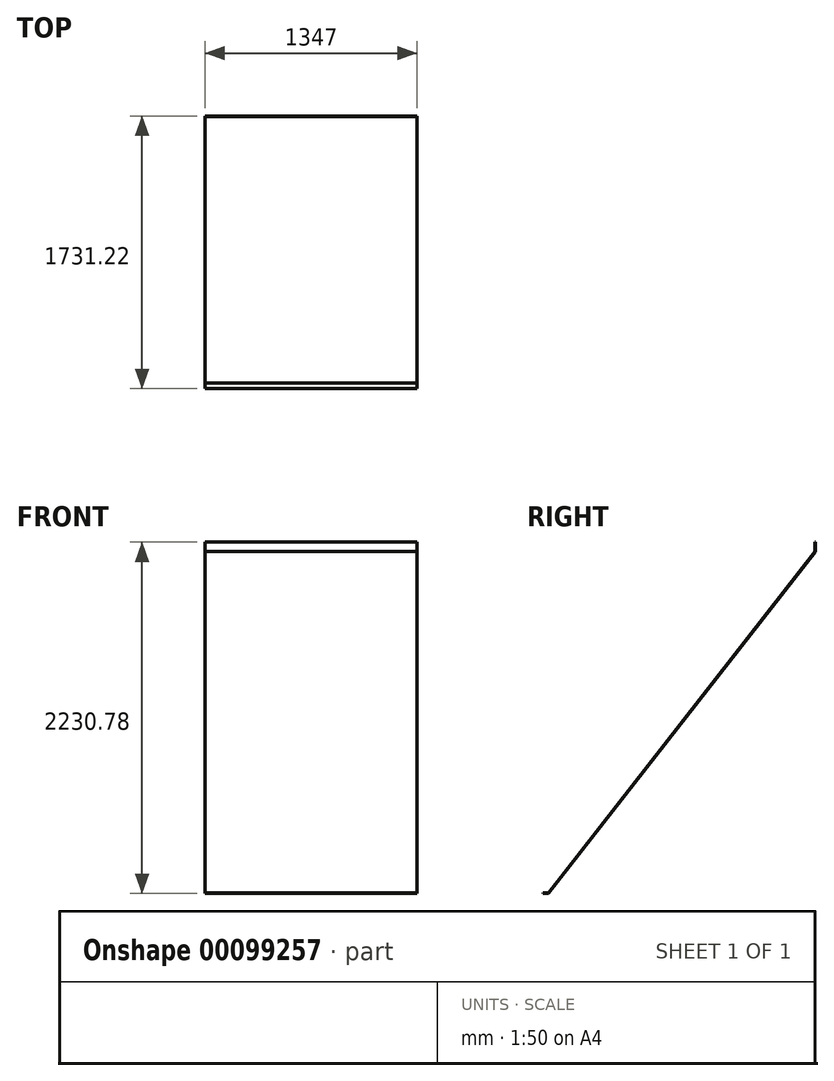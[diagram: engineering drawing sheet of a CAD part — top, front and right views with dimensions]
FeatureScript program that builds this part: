
annotation { "Feature Type Name" : "Feature", "Feature Type Description" : "" }
export const myFeature = defineFeature(function(context is Context, id is Id, definition is map)
    precondition{}
    {
        {
            var Q0;
            Q0=qCreatedBy(makeId("Right.planeOp"),FACE);
            var sketch = newSketch(context, id + "F0", { "sketchPlane" : qUnion([Q0])});
            skLineSegment(sketch, "E0", {"start": v(-36, 0) * mm, "end": v(0, 0) * mm});
            skLineSegment(sketch, "E1", {"start": v(0, 0) * mm, "end": v(1695.22, 2169.78) * mm});
            skLineSegment(sketch, "E2", {"start": v(1695.22, 2169.78) * mm, "end": v(1695.22, 2230.78) * mm});
            skLineSegment(sketch, "E3.0", {"start": v(-1.46, 3) * mm, "end": v(1692.22, 2170.82) * mm});
            skLineSegment(sketch, "E4.0", {"start": v(1692.22, 2170.82) * mm, "end": v(1692.22, 2230.78) * mm});
            skLineSegment(sketch, "E5.0", {"start": v(-36, 3) * mm, "end": v(-1.46, 3) * mm});
            skLineSegment(sketch, "E6", {"start": v(-36, 0) * mm, "end": v(-36, 3) * mm});
            skLineSegment(sketch, "E7", {"start": v(1695.22, 2230.78) * mm, "end": v(1692.22, 2230.78) * mm});
            skSolve(sketch);
        }
        {
            var Q0;
            Q0=makeQuery(id+"F0.imprint","IMPRINT",FACE,{"disambiguationData":[TD([[makeQuery(id+"F0.imprint","IMPRINT",EDGE,{"derivedFrom":sQuery(id+"F0.wireOp",EDGE,"E0")}),1.0]])]});
            extrude(context, id + "F1", {"entities" : qUnion([Q0]), "depth" : 1347 * mm});
        }
    });
